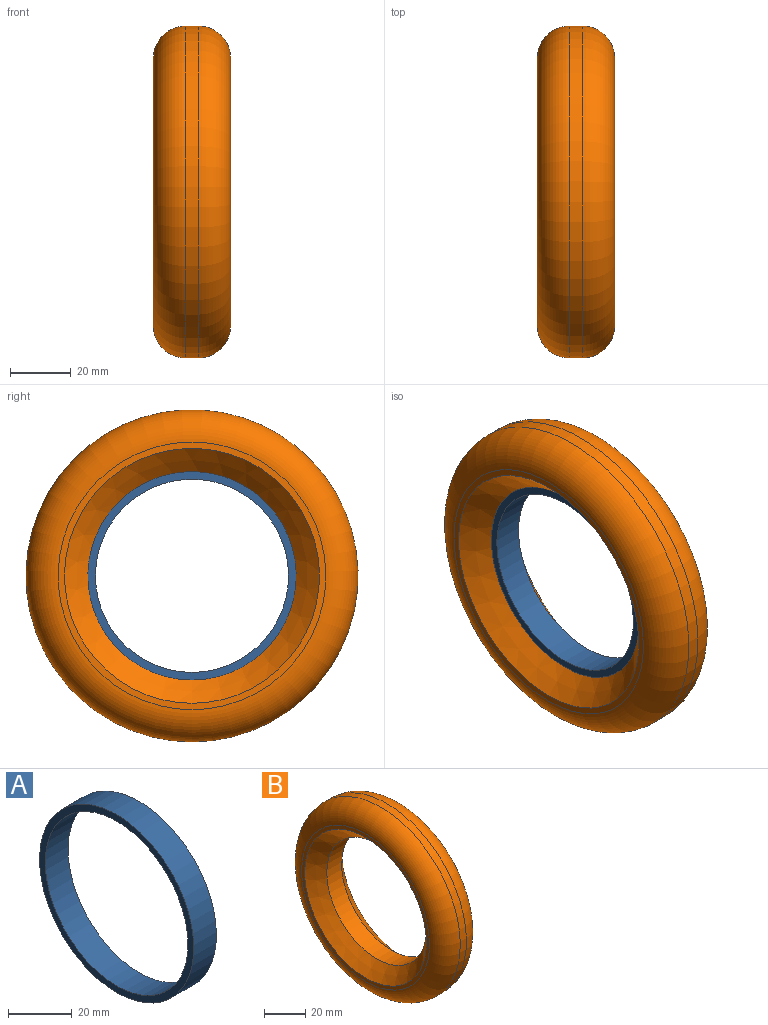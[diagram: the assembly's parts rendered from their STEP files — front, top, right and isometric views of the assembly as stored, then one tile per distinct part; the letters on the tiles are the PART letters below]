
ASSEMBLY  parts=2 mates=1
PART A: 4 faces, bbox 10.1x68.6x68.6 mm
  f0: cylinder r=31.75mm len=63.5mm, axis (-1,0,0), area 2015.2mm2, adj f2,f3
  f1: cylinder r=34.29mm len=68.58mm, axis (-1,0,0), area 2176.4mm2, adj f2,f3
  f2: plane 68.58x68.58mm, normal (1,0,0), area 527mm2, adj f0,f1
  f3: plane 68.58x68.58mm, normal (-1,0,0), area 527mm2, adj f0,f1
PART B: 8 faces, bbox 25.4x118.2x118.2 mm
  f0: cylinder r=34.29mm len=68.58mm, axis (-1,0,0), area 2189mm2, adj f6,f7
  f1: cylinder r=54.61mm len=109.22mm, axis (-1,0,0), area 1444.7mm2, adj f4,f5
  f2: plane 88.03x88.03mm, normal (1,0,0), area 568.3mm2, adj f5,f6
  f3: plane 88.03x88.03mm, normal (-1,0,0), area 568.3mm2, adj f4,f7
  f4: torus R=44.02mm, axis (1,0,0), area 5307.8mm2, adj f1,f3
  f5: torus R=44.02mm, axis (1,0,0), area 5307.8mm2, adj f1,f2
  f6: cone r=34.29mm half-angle=45deg, axis (1,0,0), area 2579.7mm2, adj f0,f2
  f7: cone r=41.91mm half-angle=45deg, axis (-1,0,0), area 2579.7mm2, adj f0,f3
PLACE A t=(7.56,0,0)mm
PLACE B at identity
MATE slider A.f0 <-> B.f0  axis (-1,0,0) through (7.62,0,0)mm
